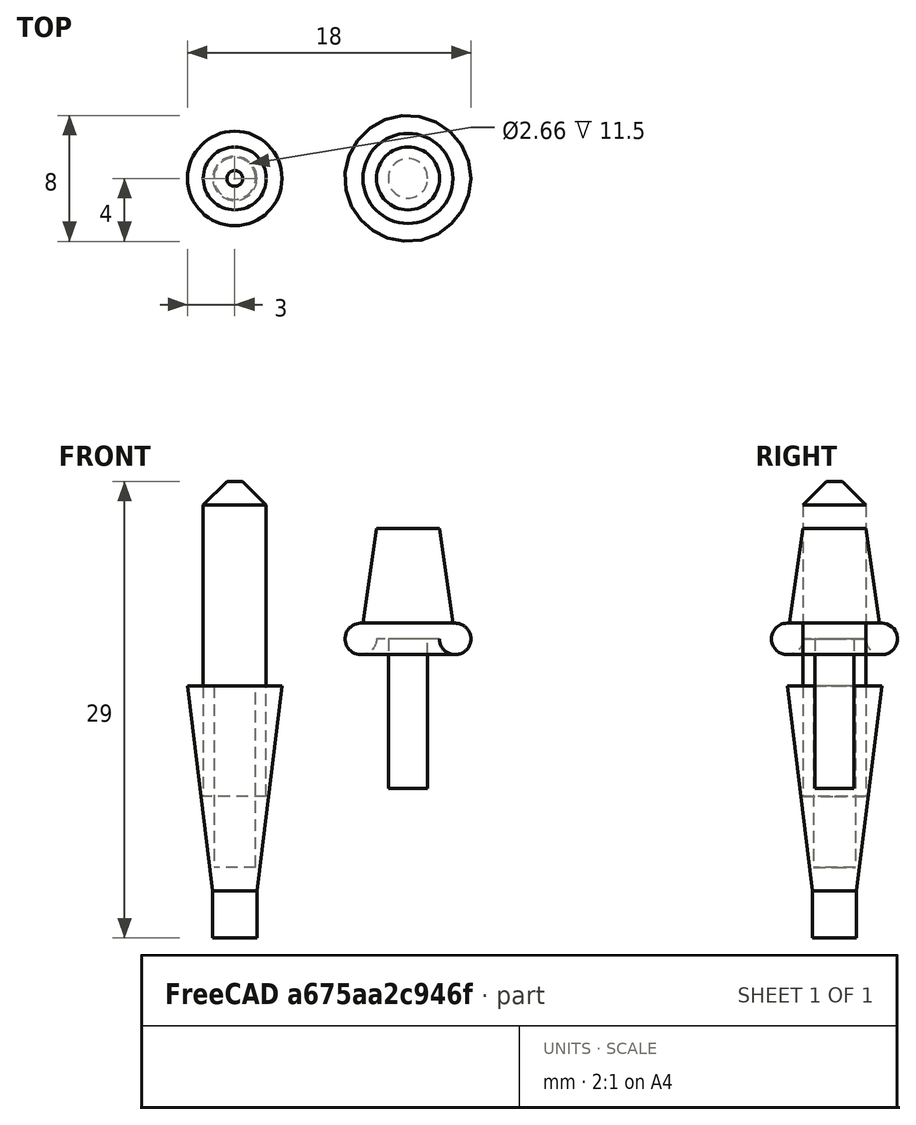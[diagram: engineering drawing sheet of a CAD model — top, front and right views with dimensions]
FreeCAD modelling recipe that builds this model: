
FCSTD DOCUMENT  (FreeCAD 1.0R39109 (Git))
Label: CribbagePeg
License: All rights reserved
LicenseURL: http://en.wikipedia.org/wiki/All_rights_reserved
objects: Part::Cylinder×4, Part::Cone×2, Part::MultiFuse×2, Part::Chamfer×1, Part::Torus×1, Part::Cut×1
note: 11 computed .brp shape members not serialized (recipe doc carries the construction recipe); baked Part::Feature solids carry a one-line shape summary decoded from their .brp

FEATURE [Part::Cone] Cone008
  Angle = 360
  AttacherType = Attacher::AttachEngine3D
  Height = 13
  Placement = pos=(-39,0,0) rot=(0,0,1;0rad)
  Radius1 = 1.4
  Radius2 = 3
FEATURE [Part::Cylinder] Cylinder009  label="MagnetCavity005"
  Angle = 360
  AttacherType = Attacher::AttachEngine3D
  FirstAngle = 0
  Height = 20
  Placement = pos=(-39,0,18) rot=(0,0,1;0rad)
  Radius = 2
  SecondAngle = 0
FEATURE [Part::Cylinder] Cylinder010  label="PegMount"
  Angle = 360
  AttacherType = Attacher::AttachEngine3D
  FirstAngle = 0
  Height = 3
  Placement = pos=(-39,0,-3) rot=(0,0,1;0rad)
  Radius = 1.4
  SecondAngle = 0
FEATURE [Part::Chamfer] Chamfer
  Base = -> Cylinder009
  EdgeLinks = -> Cylinder009 [Edge3]
  Edges = 1 edges r=1.5: [Edge3]
  Placement = pos=(0,0,-12) rot=(0,0,1;0rad)
FEATURE [Part::Cylinder] Cylinder011  label="MagnetCavity006"
  Angle = 360
  AttacherType = Attacher::AttachEngine3D
  FirstAngle = 0
  Height = 20
  Placement = pos=(-39,0,1.5) rot=(0,0,1;0rad)
  Radius = 1.33
  SecondAngle = 0
FEATURE [Part::Cylinder] Cylinder012  label="CavityInsert001"
  Angle = 360
  AttacherType = Attacher::AttachEngine3D
  FirstAngle = 0
  Height = 11
  Placement = pos=(6,0,6.5) rot=(0,0,1;0rad)
  Radius = 1.25
  SecondAngle = 0
FEATURE [Part::Torus] Torus001
  Angle1 = -180
  Angle2 = 180
  Angle3 = 360
  AttacherType = Attacher::AttachEngine3D
  Placement = pos=(6,0,16) rot=(0,0,1;0rad)
  Radius1 = 3
  Radius2 = 1
FEATURE [Part::Cone] Cone009
  Angle = 360
  AttacherType = Attacher::AttachEngine3D
  Height = 7
  Placement = pos=(6,0,23) rot=(0,1,0;3.14159rad)
  Radius1 = 2
  Radius2 = 3
FEATURE [Part::MultiFuse] Fusion
  Placement = pos=(-34,0,0) rot=(0,0,1;0rad)
  Shapes = -> [Cylinder012,Cone009,Torus001]
FEATURE [Part::Cut] Cut
  Base = -> Cone008
  Tool = -> Cylinder011
FEATURE [Part::MultiFuse] Fusion001
  Shapes = -> [Cylinder010,Cut]
